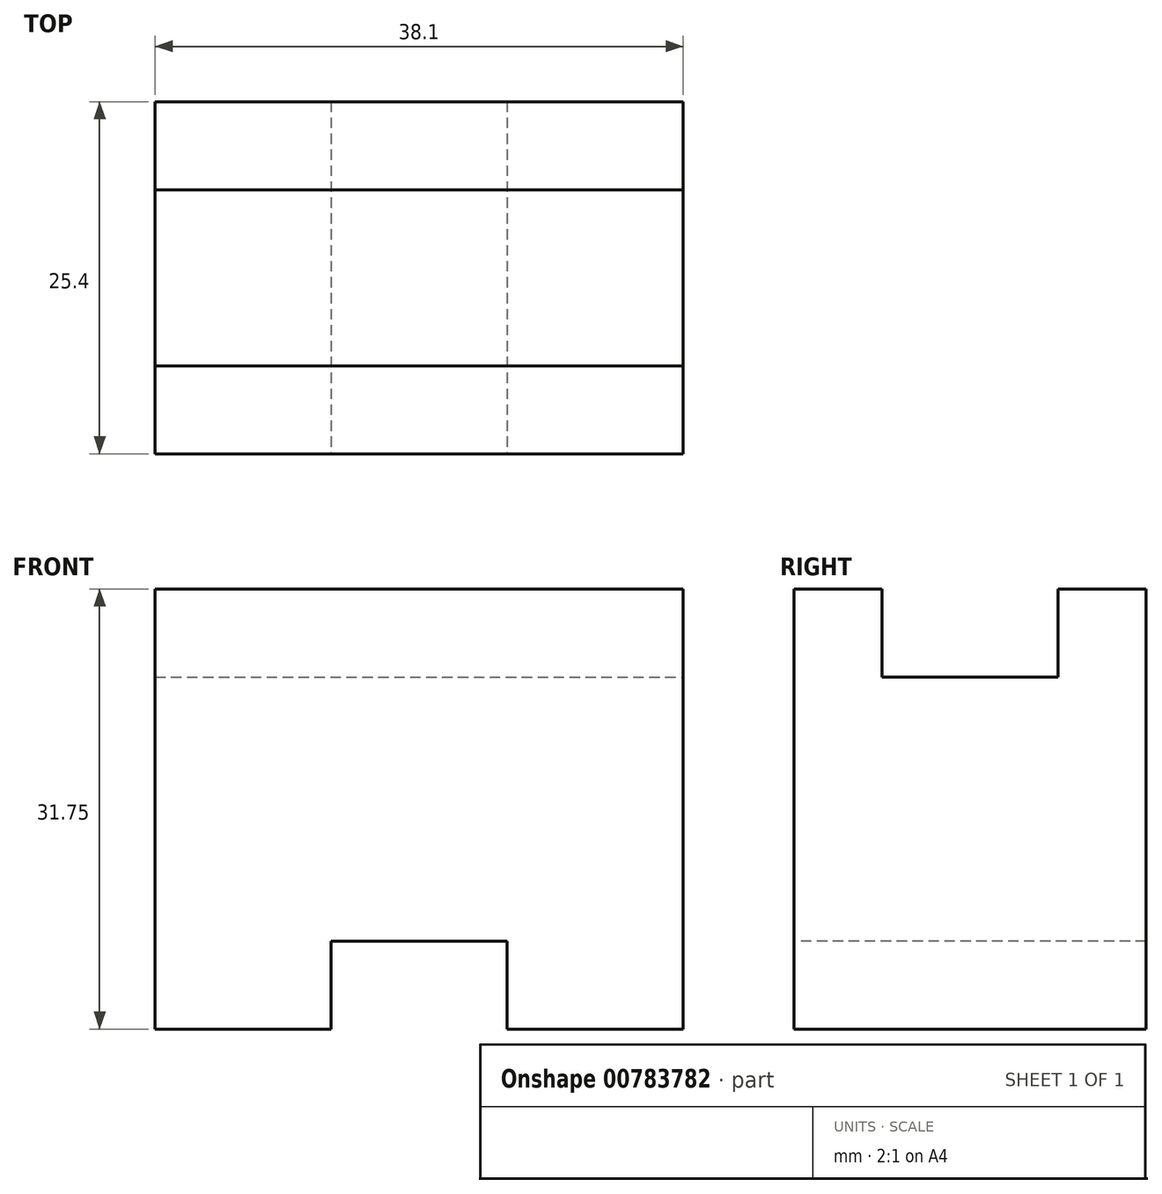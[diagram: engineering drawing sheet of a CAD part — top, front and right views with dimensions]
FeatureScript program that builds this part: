
annotation { "Feature Type Name" : "Feature", "Feature Type Description" : "" }
export const myFeature = defineFeature(function(context is Context, id is Id, definition is map)
    precondition{}
    {
        {
            var Q0;
            Q0=qCreatedBy(makeId("Right.planeOp"),FACE);
            var sketch = newSketch(context, id + "F0", { "sketchPlane" : qUnion([Q0])});
            skLineSegment(sketch, "E0", {"start": v(2.33, 0) * mm, "end": v(27.73, 0) * mm});
            skLineSegment(sketch, "E1", {"start": v(27.73, 0) * mm, "end": v(27.73, 31.75) * mm});
            skLineSegment(sketch, "E2", {"start": v(27.73, 31.75) * mm, "end": v(2.33, 31.75) * mm});
            skLineSegment(sketch, "E3", {"start": v(2.33, 31.75) * mm, "end": v(2.33, 0) * mm});
            skSolve(sketch);
        }
        {
            var Q0;
            Q0=makeQuery(id+"F0.imprint","IMPRINT",FACE,{"disambiguationData":[TD([[makeQuery(id+"F0.imprint","IMPRINT",EDGE,{"derivedFrom":sQuery(id+"F0.wireOp",EDGE,"E0")}),1.0]])]});
            extrude(context, id + "F1", {"entities" : qUnion([Q0]), "depth" : 38.1 * mm, "offsetDistance" : 25.4 * mm});
        }
        {
            var Q0;
            Q0=makeQuery(id+"F1.opExtrude","CAP_FACE",FACE,{"disambiguationData":[OSD([sQuery(id+"F0.wireOp",EDGE,"E0"),sQuery(id+"F0.wireOp",EDGE,"E1"),sQuery(id+"F0.wireOp",EDGE,"E2"),sQuery(id+"F0.wireOp",EDGE,"E3")])],"isStart":false});
            var sketch = newSketch(context, id + "F2", { "sketchPlane" : qUnion([Q0])});
            skLineSegment(sketch, "E4", {"start": v(2.33, 31.75) * mm, "end": v(8.68, 31.75) * mm});
            skLineSegment(sketch, "E5", {"start": v(8.68, 31.75) * mm, "end": v(8.68, 25.4) * mm});
            skLineSegment(sketch, "E6", {"start": v(8.68, 25.4) * mm, "end": v(21.38, 25.4) * mm});
            skLineSegment(sketch, "E7", {"start": v(21.38, 25.4) * mm, "end": v(21.38, 31.75) * mm});
            skSolve(sketch);
        }
        {
            var Q0;
            {var subQ0=sQuery(id+"F2.wireOp",EDGE,"E5");Q0=makeQuery(id+"F2.imprint","IMPRINT",FACE,{"disambiguationData":[TD([[makeQuery(id+"F2.imprint","IMPRINT",EDGE,{"derivedFrom":subQ0}),1.0]])]});}
            extrude(context, id + "F3", {"entities" : qUnion([Q0]), "operationType" : NewBodyOperationType.REMOVE, "oppositeDirection" : true, "depth" : 38.1 * mm, "offsetDistance" : 25.4 * mm});
        }
        {
            var Q0;
            Q0=makeQuery(id+"F1.opExtrude","SWEPT_FACE",FACE,{"disambiguationData":[OSD([sQuery(id+"F0.wireOp",EDGE,"E3")])]});
            var sketch = newSketch(context, id + "F4", { "sketchPlane" : qUnion([Q0])});
            skLineSegment(sketch, "E8", {"start": v(0, 0) * mm, "end": v(12.7, 0) * mm});
            skLineSegment(sketch, "E9", {"start": v(12.7, 0) * mm, "end": v(12.7, 6.35) * mm});
            skLineSegment(sketch, "E10", {"start": v(12.7, 6.35) * mm, "end": v(25.4, 6.35) * mm});
            skLineSegment(sketch, "E11", {"start": v(25.4, 6.35) * mm, "end": v(25.4, 0) * mm});
            skSolve(sketch);
        }
        {
            var Q0;
            {var subQ0=sQuery(id+"F4.wireOp",EDGE,"E9");Q0=makeQuery(id+"F4.imprint","IMPRINT",FACE,{"disambiguationData":[TD([[makeQuery(id+"F4.imprint","IMPRINT",EDGE,{"derivedFrom":subQ0}),-1.0]])]});}
            extrude(context, id + "F5", {"entities" : qUnion([Q0]), "operationType" : NewBodyOperationType.REMOVE, "oppositeDirection" : true, "depth" : 25.4 * mm, "offsetDistance" : 25.4 * mm});
        }
    });
